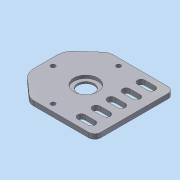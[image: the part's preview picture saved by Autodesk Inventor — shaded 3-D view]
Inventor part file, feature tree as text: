
AUTODESK INVENTOR PART (.ipt)
format: ipt  version: 2013 (Build 170138000, 138)  size: 179,200 bytes
history: native  units: mm
features: fillet x4, sketch x4, extrude x2, hole x2, pattern_linear x1
ambient origin geometry x8: Origin, YZ Plane, XZ Plane, XY Plane, X Axis, Y Axis, Z Axis, Center Point
bodies: Solid1 (feature_tree)
feature tree (13):
  extrude  "Extrusion1"  Depth=53.0mm
  extrude  "Extrusion2"  Depth=21.36mm
  pattern_linear  "Rectangular Pattern1"  Spacing1=12.458078mm  [1 undecoded]
  hole  "Hole1"  [1 undecoded]
  hole  "Hole2"  [1 undecoded]
  fillet  "Fillet1"  Radius=59.29mm
  fillet  "Fillet2"  Radius=3.17mm
  fillet  "Fillet3"  Radius=6.49mm
  fillet  "Fillet4"  Radius=6.81mm
  sketch  "Sketch1"  dims[d0=59.29mm d2=53.0mm]
  sketch  "Sketch2"  dims[d3=14.5mm d4=21.36mm]
  sketch  "Sketch3"  dims[d6=7.68mm]
  sketch  "Sketch4"  dims[d7=41.75mm d8=12.458078mm d9=12.458078mm d10=43.581594mm d11=59.29mm d12=3.17mm d13=0.0mm d14=6.49mm d15=6.81mm d16=5.0mm d17=11.81mm d18=43.86mm d19=3.17mm d20=0.0mm d21=50.0mm d23=10.0mm d24=26.86mm d25=11.0mm d26=6.0mm d27=16.05mm d28=2.0mm d29=90.0deg d30=8.0mm d31=20.594885mm d34=26.86mm d35=43.82mm d36=21.91mm d37=4.96mm d38=21.9mm d39=3.0mm d40=6.0mm d41=16.05mm d42=2.0mm d43=90.0deg d44=8.0mm d45=20.594885mm d46=7.25mm d47=7.25mm d48=10.68mm d49=4.0mm]
note: 3 required parameter values undecoded (feature->parameter linkage not recoverable at this tier; creation-order binding heuristic only, values carry confidence <= 0.55)
